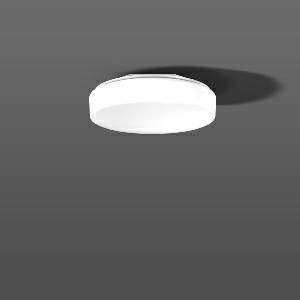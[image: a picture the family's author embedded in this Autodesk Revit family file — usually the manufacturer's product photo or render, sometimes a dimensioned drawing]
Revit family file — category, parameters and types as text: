
# Revit family: flat_polymero_kreis_672478_002_1_2e81
name_source: partatom
category: Lighting Fixtures
units: mm (PartAtom-declared; Revit-internal decimal feet)

## family parameters
Cut with Voids When Loaded = No
Host = Face
Light Source = No
Part Type = Normal
Room Calculation Point = No
Round Connector Dimension = Use Diameter
Shared = No

## types (1)
- FLAT POLYMERO KREIS (1 x LED Modul 840, 1200 lm, 4000)
    Apparent Load = 13 VA
    CIE Flux Codes = 41 72 91 84 100
    Color Rendering = 80
    Color Temperature = 4000
    Default Elevation = 1800 mm
    Description = Series: FLAT POLYMERO KREIS
Decorative round surface-mounted luminaire. For escape route illumination. Base: metal, powder-coated. Diffuser made of non-yellowing plastic (PMMA), opal. Diffuser fastening: patented push system. Suitable for Ceiling mounting, Wall (surface). Electronic ballast included. Self-contained system with automatic self-test. 
Colour: white
Diameter: 360 mm
Height: 87 mm
Weight: 1.44 kg
Operating mode: Combined NL readiness
Duration time: 3 h
Lamp: LED
Socket: without socket
Colour temperature: 4000K
Colour rendering index (CRI): 80
System power: 13 W
Rated luminous flux: 1200 lm
Luminous flux, emergency: 170 lm
System power, emergency: -
Control gear: Converter not necessary
Protection class: I
Type of protection: IP 40
    Height = 87 mm
    Lamp = 1 x LED Modul 840
    Lamp Light Flux = 1200 lm
    Lamp count = 1
    Length = 360 mm
    Lifetime = 50000 h
    Luminous efficacy = 92 lm/W
    Manufacturer = RZB
    ModVariant = No
    Model = 672478.002.1
    Mounting Place = Ceiling, Wall
    Mounting Type = Surface mounted
    Number of Poles = 1
    OnlyDefault = Yes
    Power Factor = 1
    Product Name = FLAT POLYMERO KREIS
    Product group = Surface mounted ceiling and wall luminaires
    ProductGroupID = 305
    Protection Class = Protection class I
    Protection Degree = IP 40
    RLX_Detail_Level = 1
    RLX_Emergency_Light_Flux = 170 lm
    RLX_Emergency_Type = 3
    RLX_Emergency_Type_DB = Yes
    RlxData = <blob elided: 52117 chars, md5=8e469458>
    Socket = socket
    Standby Power = 0 W
    System Light Flux = 1200 lm
    System Power = 13 W
    Type Comments = Product without accessories
    Type Image = 672092.002.1.jpg
    URL = http://relux.com
    VarID = ---
    Voltage = 230 V
    Voltage Range = 220-240 V
    Weight = 0.00 kg
    Width = 0 mm  [stored 0 ft]

note: [stored X ft] marks values corroborated as IEEE doubles in the binary element streams (Revit-internal decimal feet)

## geometry (parser evidence)
native form markers: Blend x4, Sweep x13
no freeform markers — native parametric forms only
